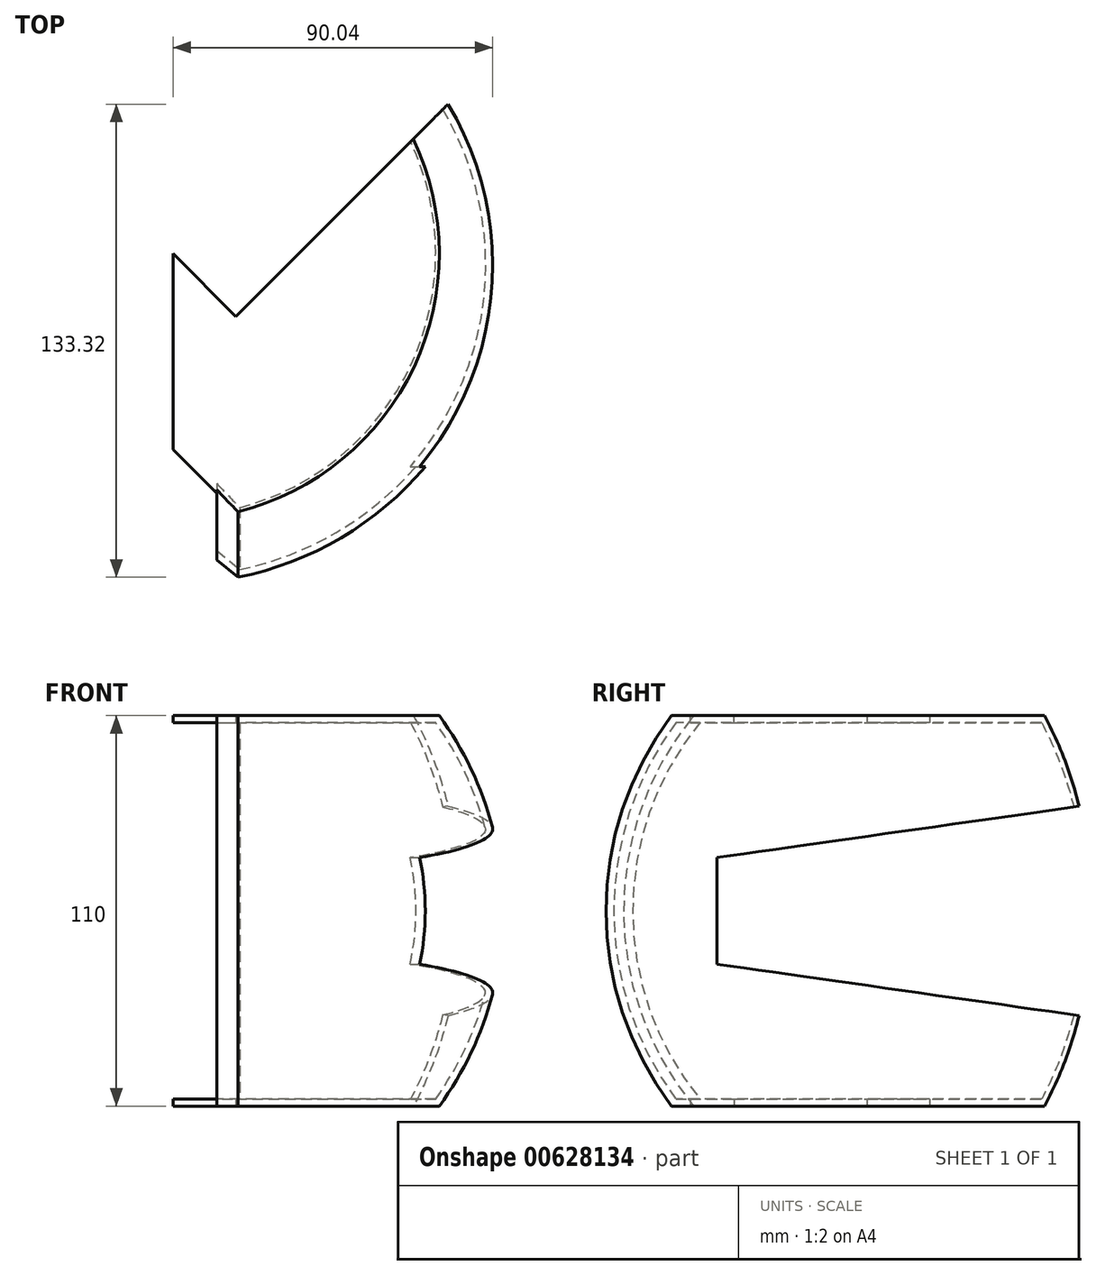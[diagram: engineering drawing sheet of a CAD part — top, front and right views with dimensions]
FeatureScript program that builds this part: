
annotation { "Feature Type Name" : "Feature", "Feature Type Description" : "" }
export const myFeature = defineFeature(function(context is Context, id is Id, definition is map)
    precondition{}
    {
        {
            var Q0;
            Q0=qCreatedBy(makeId("Right.planeOp"),FACE);
            var sketch = newSketch(context, id + "F0", { "sketchPlane" : qUnion([Q0])});
            skLineSegment(sketch, "E0", {"start": v(0, 0) * mm, "end": v(0, 55) * mm});
            skLineSegment(sketch, "E1", {"start": v(0, 55) * mm, "end": v(-75, 55) * mm});
            skArc(sketch, "E2", {"start": v(-75, 55) * mm, "mid": v(-93, 0) * mm, "end": v(-75, -55) * mm});
            skLineSegment(sketch, "E3.MirrorCS", {"start": v(0, -55) * mm, "end": v(-75, -55) * mm});
            skLineSegment(sketch, "E4.MirrorCS", {"start": v(0, 0) * mm, "end": v(0, -55) * mm});
            skSolve(sketch);
        }
        {
            var Q0;
            Q0=makeQuery(id+"F0.imprint","IMPRINT",FACE,{"disambiguationData":[TD([[makeQuery(id+"F0.imprint","IMPRINT",EDGE,{"derivedFrom":sQuery(id+"F0.wireOp",EDGE,"E0")}),1.0]])]});
            var Q1;
            Q1=sQuery(id+"F0.wireOp",EDGE,"E0");
            revolve(context, id + "F1", {"entities" : qUnion([Q0]), "axis" : qUnion([Q1]), "revolveType" : RevolveType.ONE_DIRECTION, "angle" : 180 * degree});
        }
        {
            var Q0;
            Q0=makeQuery(id+"F1.opRevolve","SWEPT_FACE",FACE,{"disambiguationData":[OSD([sQuery(id+"F0.wireOp",EDGE,"E3.MirrorCS")])]});
            var sketch = newSketch(context, id + "F2", { "sketchPlane" : qUnion([Q0])});
            skLineSegment(sketch, "E5", {"start": v(0, 0) * mm, "end": v(0, 40) * mm});
            skLineSegment(sketch, "E6", {"start": v(0, 40) * mm, "end": v(12.29, 48.6) * mm});
            skLineSegment(sketch, "E7", {"start": v(12.29, 48.6) * mm, "end": v(12.29, 106.32) * mm});
            skLineSegment(sketch, "E8", {"start": v(0, 0) * mm, "end": v(17.68, 17.68) * mm});
            skLineSegment(sketch, "E9", {"start": v(17.68, 17.68) * mm, "end": v(82.74, -47.39) * mm});
            skLineSegment(sketch, "E10", {"start": v(12.29, 106.32) * mm, "end": v(-66.16, 106.32) * mm});
            skLineSegment(sketch, "E11", {"start": v(-66.16, 106.32) * mm, "end": v(-66.16, -110.8) * mm});
            skLineSegment(sketch, "E12", {"start": v(-66.16, -110.8) * mm, "end": v(82.74, -110.8) * mm});
            skLineSegment(sketch, "E13", {"start": v(82.74, -110.8) * mm, "end": v(82.74, -47.39) * mm});
            skSolve(sketch);
        }
        {
            var Q0;
            {var subQ0=sQuery(id+"F2.wireOp",EDGE,"E6");Q0=makeQuery(id+"F2.imprint","IMPRINT",FACE,{"disambiguationData":[TD([[makeQuery(id+"F2.imprint","IMPRINT",EDGE,{"derivedFrom":subQ0}),1.0]])]});}
            var Q1;
            {var subQ10=sQuery(id+"F2.wireOp",EDGE,"E5");Q1=makeQuery(id+"F2.imprint","IMPRINT",FACE,{"disambiguationData":[TD([[makeQuery(id+"F2.imprint","IMPRINT",EDGE,{"derivedFrom":subQ10}),-1.0]])]});}
            var Q2;
            {var subQ0=sQuery(id+"F2.wireOp",EDGE,"E8");Q2=makeQuery(id+"F2.imprint","IMPRINT",FACE,{"disambiguationData":[TD([[makeQuery(id+"F2.imprint","IMPRINT",EDGE,{"derivedFrom":subQ0}),-1.0]])]});}
            extrude(context, id + "F3", {"entities" : qUnion([Q0, Q1, Q2]), "operationType" : NewBodyOperationType.REMOVE, "endBound" : BoundingType.THROUGH_ALL, "oppositeDirection" : true, "depth" : 25 * mm, "offsetDistance" : 25 * mm});
        }
        {
            var Q0;
            Q0=qCreatedBy(makeId("Right.planeOp"),FACE);
            cPlane(context, id + "F4", {"entities" : qUnion([Q0]), "cplaneType" : CPlaneType.OFFSET, "offset" : 100 * mm, "width" : 150 * mm, "height" : 150 * mm});
        }
        {
            var Q0;
            Q0=qCreatedBy(id+"F4.planeOp",FACE);
            var sketch = newSketch(context, id + "F5", { "sketchPlane" : qUnion([Q0])});
            skLineSegment(sketch, "E14", {"start": v(45.67, 30) * mm, "end": v(45.67, -30) * mm});
            skLineSegment(sketch, "E15", {"start": v(-60, 0) * mm, "end": v(-60, 15) * mm});
            skLineSegment(sketch, "E16", {"start": v(0, 0) * mm, "end": v(45.67, 0) * mm});
            skLineSegment(sketch, "E17", {"start": v(-60, 15) * mm, "end": v(45.67, 30) * mm});
            skLineSegment(sketch, "E18.MirrorCS", {"start": v(-60, 0) * mm, "end": v(-60, -15) * mm});
            skLineSegment(sketch, "E19.MirrorCS", {"start": v(-60, -15) * mm, "end": v(45.67, -30) * mm});
            skSolve(sketch);
        }
        {
            var Q0;
            Q0 = qSketchRegion(id + "F5", true);
            extrude(context, id + "F6", {"entities" : qUnion([Q0]), "operationType" : NewBodyOperationType.REMOVE, "endBound" : BoundingType.THROUGH_ALL, "oppositeDirection" : true, "depth" : 25 * mm, "offsetDistance" : 25 * mm});
        }
        {
            var Q0;
            Q0=makeQuery(id+"F3.boolean.opBoolean","INTERSECT",EDGE,{"derivedFrom":[makeQuery(id+"F1.opRevolve","SWEPT_FACE",FACE,{"disambiguationData":[OSD([sQuery(id+"F0.wireOp",EDGE,"E2")])]}),makeQuery(id+"F3.opExtrude","SWEPT_FACE",FACE,{"disambiguationData":[OSD([sQuery(id+"F2.wireOp",EDGE,"E7")])]})]});
            chamfer(context, id + "F7", {"entities" : qUnion([Q0]), "width" : 5 * mm, "tangentPropagation" : true});
        }
        {
            var Q0;
            Q0=makeQuery(id+"F6.boolean.opBoolean","SPLIT",FACE,{"disambiguationData":[TD([makeQuery(id+"F1.opRevolve","SWEPT_FACE",FACE,{"disambiguationData":[OSD([sQuery(id+"F0.wireOp",EDGE,"E3.MirrorCS")])]})])],"derivedFrom":makeQuery(id+"F3.boolean.opBoolean","COPY",FACE,{"derivedFrom":makeQuery(id+"F3.opExtrude","SWEPT_FACE",FACE,{"disambiguationData":[OSD([sQuery(id+"F2.wireOp",EDGE,"E9")])]})})});
            var Q1;
            {var subQ0=sQuery(id+"F0.wireOp",EDGE,"E3.MirrorCS");Q1=makeQuery(id+"F6.boolean.opBoolean","SPLIT",FACE,{"disambiguationData":[TD([makeQuery(id+"F1.opRevolve","SWEPT_FACE",FACE,{"disambiguationData":[OSD([subQ0])]})])],"derivedFrom":makeQuery(id+"F3.boolean.opBoolean","COPY",FACE,{"derivedFrom":makeQuery(id+"F3.opExtrude","SWEPT_FACE",FACE,{"disambiguationData":[OSD([sQuery(id+"F2.wireOp",EDGE,"E8")])]})})});}
            var Q2;
            {var subQ0=sQuery(id+"F0.wireOp",EDGE,"E3.MirrorCS");Q2=makeQuery(id+"F6.boolean.opBoolean","SPLIT",FACE,{"disambiguationData":[TD([makeQuery(id+"F1.opRevolve","SWEPT_FACE",FACE,{"disambiguationData":[OSD([subQ0])]})])],"derivedFrom":makeQuery(id+"F1.opRevolve","CAP_FACE",FACE,{"disambiguationData":[OSD([sQuery(id+"F0.wireOp",EDGE,"E0"),sQuery(id+"F0.wireOp",EDGE,"E1"),sQuery(id+"F0.wireOp",EDGE,"E2"),subQ0,sQuery(id+"F0.wireOp",EDGE,"E4.MirrorCS")])],"isStart":false})});}
            var Q3;
            Q3=makeQuery(id+"F6.boolean.opBoolean","COPY",FACE,{"derivedFrom":makeQuery(id+"F6.opExtrude","SWEPT_FACE",FACE,{"disambiguationData":[OSD([sQuery(id+"F5.wireOp",EDGE,"E19.MirrorCS")])]})});
            var Q4;
            Q4=makeQuery(id+"F6.boolean.opBoolean","COPY",FACE,{"derivedFrom":makeQuery(id+"F6.opExtrude","SWEPT_FACE",FACE,{"disambiguationData":[OSD([sQuery(id+"F5.wireOp",EDGE,"E17")])]})});
            var Q5;
            Q5=makeQuery(id+"F6.boolean.opBoolean","SPLIT",FACE,{"disambiguationData":[TD([makeQuery(id+"F1.opRevolve","SWEPT_FACE",FACE,{"disambiguationData":[OSD([sQuery(id+"F0.wireOp",EDGE,"E1")])]})])],"derivedFrom":makeQuery(id+"F3.boolean.opBoolean","COPY",FACE,{"derivedFrom":makeQuery(id+"F3.opExtrude","SWEPT_FACE",FACE,{"disambiguationData":[OSD([sQuery(id+"F2.wireOp",EDGE,"E9")])]})})});
            var Q6;
            {var subQ0=sQuery(id+"F0.wireOp",EDGE,"E1");Q6=makeQuery(id+"F6.boolean.opBoolean","SPLIT",FACE,{"disambiguationData":[TD([makeQuery(id+"F1.opRevolve","SWEPT_FACE",FACE,{"disambiguationData":[OSD([subQ0])]})])],"derivedFrom":makeQuery(id+"F3.boolean.opBoolean","COPY",FACE,{"derivedFrom":makeQuery(id+"F3.opExtrude","SWEPT_FACE",FACE,{"disambiguationData":[OSD([sQuery(id+"F2.wireOp",EDGE,"E8")])]})})});}
            var Q7;
            {var subQ0=sQuery(id+"F0.wireOp",EDGE,"E1");Q7=makeQuery(id+"F6.boolean.opBoolean","SPLIT",FACE,{"disambiguationData":[TD([makeQuery(id+"F1.opRevolve","SWEPT_FACE",FACE,{"disambiguationData":[OSD([subQ0])]})])],"derivedFrom":makeQuery(id+"F1.opRevolve","CAP_FACE",FACE,{"disambiguationData":[OSD([sQuery(id+"F0.wireOp",EDGE,"E0"),subQ0,sQuery(id+"F0.wireOp",EDGE,"E2"),sQuery(id+"F0.wireOp",EDGE,"E3.MirrorCS"),sQuery(id+"F0.wireOp",EDGE,"E4.MirrorCS")])],"isStart":false})});}
            var Q8;
            {var subQ0=sQuery(id+"F0.wireOp",EDGE,"E3.MirrorCS");Q8=makeQuery(id+"F6.boolean.opBoolean","SPLIT",FACE,{"disambiguationData":[TD([makeQuery(id+"F1.opRevolve","SWEPT_FACE",FACE,{"disambiguationData":[OSD([subQ0])]})])],"derivedFrom":makeQuery(id+"F3.boolean.opBoolean","COPY",FACE,{"derivedFrom":makeQuery(id+"F3.opExtrude","SWEPT_FACE",FACE,{"disambiguationData":[OSD([sQuery(id+"F2.wireOp",EDGE,"E6")])]})})});}
            var Q9;
            {var subQ0=sQuery(id+"F0.wireOp",EDGE,"E1");Q9=makeQuery(id+"F6.boolean.opBoolean","SPLIT",FACE,{"disambiguationData":[TD([makeQuery(id+"F1.opRevolve","SWEPT_FACE",FACE,{"disambiguationData":[OSD([subQ0])]})])],"derivedFrom":makeQuery(id+"F3.boolean.opBoolean","COPY",FACE,{"derivedFrom":makeQuery(id+"F3.opExtrude","SWEPT_FACE",FACE,{"disambiguationData":[OSD([sQuery(id+"F2.wireOp",EDGE,"E6")])]})})});}
            var Q10;
            Q10=makeQuery(id+"F3.boolean.opBoolean","COPY",FACE,{"derivedFrom":makeQuery(id+"F3.opExtrude","SWEPT_FACE",FACE,{"disambiguationData":[OSD([sQuery(id+"F2.wireOp",EDGE,"E7")])]})});
            var Q11;
            Q11=makeQuery(id+"F6.boolean.opBoolean","COPY",FACE,{"derivedFrom":makeQuery(id+"F6.opExtrude","SWEPT_FACE",FACE,{"disambiguationData":[OSD([sQuery(id+"F5.wireOp",EDGE,"E15"),sQuery(id+"F5.wireOp",EDGE,"E18.MirrorCS")])]})});
            shell(context, id + "F8", {"entities" : qUnion([Q0, Q1, Q2, Q3, Q4, Q5, Q6, Q7, Q8, Q9, Q10, Q11]), "thickness" : 2 * mm});
        }
        {
            var Q0;
            Q0=makeQuery(id+"F1.opRevolve","SWEPT_FACE",FACE,{"disambiguationData":[OSD([sQuery(id+"F0.wireOp",EDGE,"E3.MirrorCS")])]});
            var sketch = newSketch(context, id + "F9", { "sketchPlane" : qUnion([Q0])});
            skLineSegment(sketch, "E20", {"start": v(12.29, 67.47) * mm, "end": v(0, 55.18) * mm});
            skLineSegment(sketch, "E21", {"start": v(0, 40) * mm, "end": v(0, 55.18) * mm});
            skLineSegment(sketch, "E22", {"start": v(0, 40) * mm, "end": v(12.29, 48.6) * mm});
            skLineSegment(sketch, "E23", {"start": v(12.29, 48.6) * mm, "end": v(12.29, 67.47) * mm});
            skSolve(sketch);
        }
        {
            var Q0;
            Q0=makeQuery(id+"F9.imprint","IMPRINT",FACE,{"disambiguationData":[TD([[makeQuery(id+"F9.imprint","IMPRINT",EDGE,{"derivedFrom":sQuery(id+"F9.wireOp",EDGE,"E20")}),1.0]])]});
            extrude(context, id + "F10", {"entities" : qUnion([Q0]), "oppositeDirection" : true, "depth" : 2 * mm, "offsetDistance" : 25 * mm});
        }
        {
            var Q0;
            Q0=makeQuery(id+"F1.opRevolve","SWEPT_FACE",FACE,{"disambiguationData":[OSD([sQuery(id+"F0.wireOp",EDGE,"E1")])]});
            var Q1;
            Q1=makeQuery(id+"F1.opRevolve","SWEPT_FACE",FACE,{"disambiguationData":[OSD([sQuery(id+"F0.wireOp",EDGE,"E3.MirrorCS")])]});
            cPlane(context, id + "F11", {"entities" : qUnion([Q0, Q1]), "cplaneType" : CPlaneType.MID_PLANE, "offset" : 25 * mm, "width" : 150 * mm, "height" : 150 * mm});
        }
        {
            var Q0;
            Q0=makeQuery(id+"F10.opExtrude","SWEPT_BODY",BODY,{"disambiguationData":[OSD([sQuery(id+"F9.wireOp",EDGE,"E20"),sQuery(id+"F9.wireOp",EDGE,"E21"),sQuery(id+"F9.wireOp",EDGE,"E22"),sQuery(id+"F9.wireOp",EDGE,"E23")])]});
            var Q1;
            Q1=qCreatedBy(id+"F11.planeOp",FACE);
            mirror(context, id + "F12", {"operationType" : NewBodyOperationType.ADD, "entities" : qUnion([Q0]), "mirrorPlane" : qUnion([Q1])});
        }
        {
            var Q0;
            Q0=makeQuery(id+"F1.opRevolve","SWEPT_BODY",BODY,{"disambiguationData":[OSD([sQuery(id+"F0.wireOp",EDGE,"E0"),sQuery(id+"F0.wireOp",EDGE,"E1"),sQuery(id+"F0.wireOp",EDGE,"E2"),sQuery(id+"F0.wireOp",EDGE,"E3.MirrorCS"),sQuery(id+"F0.wireOp",EDGE,"E4.MirrorCS")])]});
            transform(context, id + "F13", {"entities" : qUnion([Q0]), "transformType" : TransformType.TRANSLATION_3D, "dx" : 0 * mm, "dy" : 0 * mm, "dz" : 0 * mm, "makeCopy" : true});
        }
        {
            var Q0;
            Q0=makeQuery(id+"F13.opPattern","COPY",BODY,{"derivedFrom":makeQuery(id+"F1.opRevolve","SWEPT_BODY",BODY,{"disambiguationData":[OSD([sQuery(id+"F0.wireOp",EDGE,"E0"),sQuery(id+"F0.wireOp",EDGE,"E1"),sQuery(id+"F0.wireOp",EDGE,"E2"),sQuery(id+"F0.wireOp",EDGE,"E3.MirrorCS"),sQuery(id+"F0.wireOp",EDGE,"E4.MirrorCS")])]}),"instanceName":"1"});
            deleteBodies(context, id + "F14", {"entities" : qUnion([Q0])});
        }
    });
